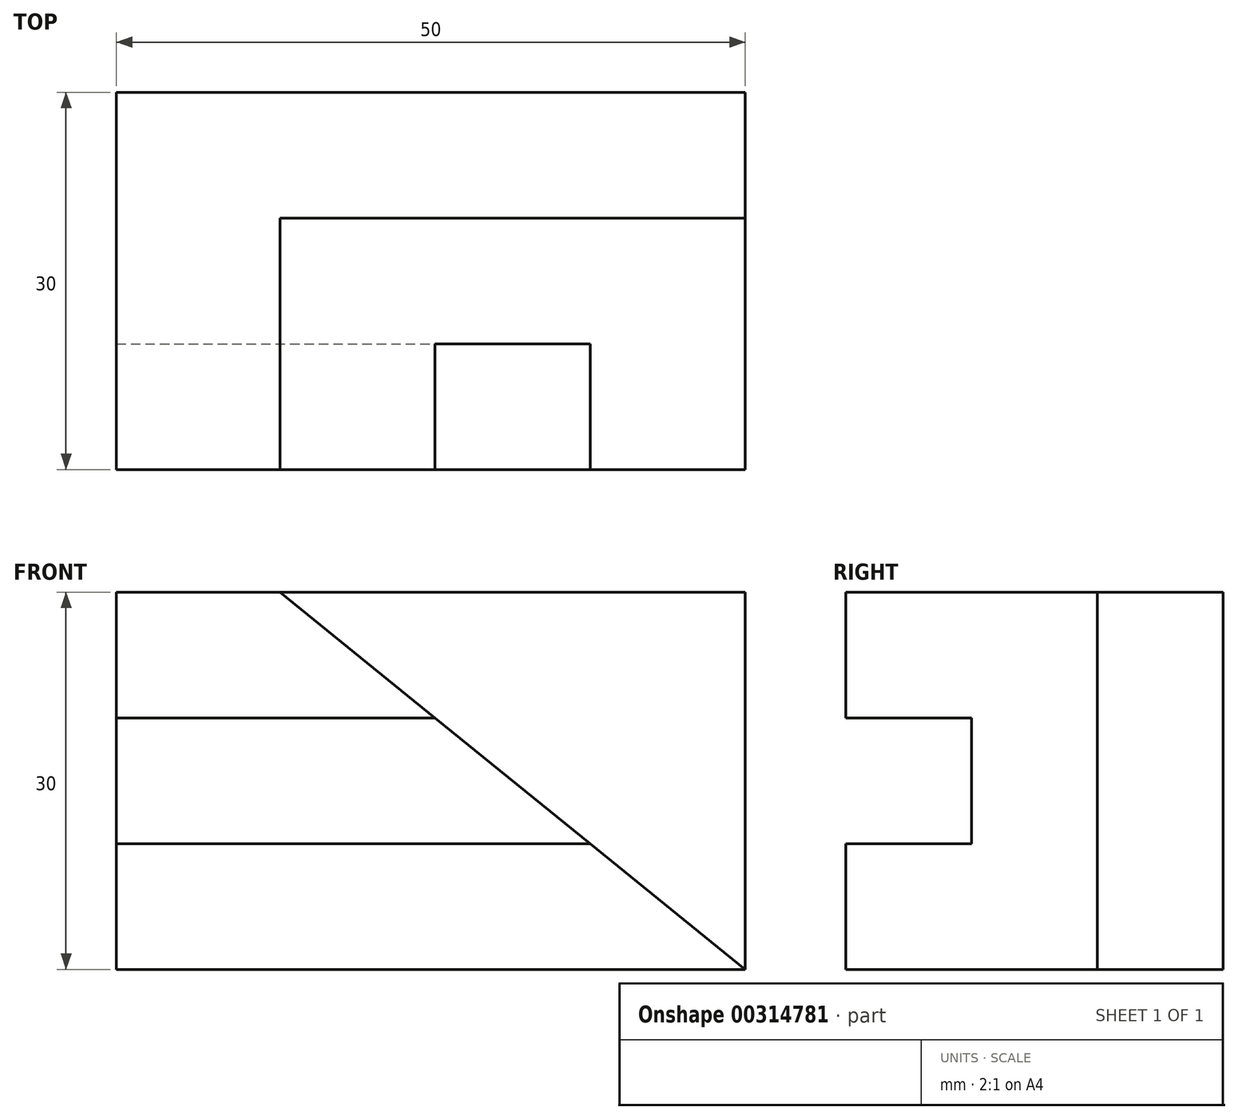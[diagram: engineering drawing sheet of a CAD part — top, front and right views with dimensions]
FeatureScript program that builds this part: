
annotation { "Feature Type Name" : "Feature", "Feature Type Description" : "" }
export const myFeature = defineFeature(function(context is Context, id is Id, definition is map)
    precondition{}
    {
        {
            var Q0;
            Q0=qCreatedBy(makeId("Front.planeOp"),FACE);
            var sketch = newSketch(context, id + "F0", { "sketchPlane" : qUnion([Q0])});
            skLineSegment(sketch, "E0.bottom", {"start": v(0, 0) * mm, "end": v(50, 0) * mm});
            skLineSegment(sketch, "E0.top", {"start": v(0, 30) * mm, "end": v(50, 30) * mm});
            skLineSegment(sketch, "E0.left", {"start": v(0, 0) * mm, "end": v(0, 30) * mm});
            skLineSegment(sketch, "E0.right", {"start": v(50, 0) * mm, "end": v(50, 30) * mm});
            skLineSegment(sketch, "E1", {"start": v(13, 30) * mm, "end": v(50, 0) * mm});
            skLineSegment(sketch, "E2", {"start": v(0, 20) * mm, "end": v(25.33, 20) * mm});
            skLineSegment(sketch, "E3", {"start": v(0, 10) * mm, "end": v(37.67, 10) * mm});
            skSolve(sketch);
        }
        {
            var Q0;
            Q0 = qSketchRegion(id + "F0", true);
            extrude(context, id + "F1", {"entities" : qUnion([Q0]), "oppositeDirection" : true, "depth" : 30 * mm});
        }
        {
            var Q0;
            {var subQ3=sQuery(id+"F0.wireOp",EDGE,"E0.right");Q0=makeQuery(id+"F0.imprint","IMPRINT",FACE,{"disambiguationData":[TD([[makeQuery(id+"F0.imprint","IMPRINT",EDGE,{"derivedFrom":subQ3}),1.0]])]});}
            extrude(context, id + "F2", {"entities" : qUnion([Q0]), "operationType" : NewBodyOperationType.REMOVE, "oppositeDirection" : true, "depth" : 20 * mm});
        }
        {
            var Q0;
            {var subQ0=sQuery(id+"F0.wireOp",EDGE,"E2");Q0=makeQuery(id+"F0.imprint","IMPRINT",FACE,{"disambiguationData":[TD([[makeQuery(id+"F0.imprint","IMPRINT",EDGE,{"derivedFrom":subQ0}),-1.0]])]});}
            extrude(context, id + "F3", {"entities" : qUnion([Q0]), "operationType" : NewBodyOperationType.REMOVE, "oppositeDirection" : true, "depth" : 10 * mm});
        }
    });
